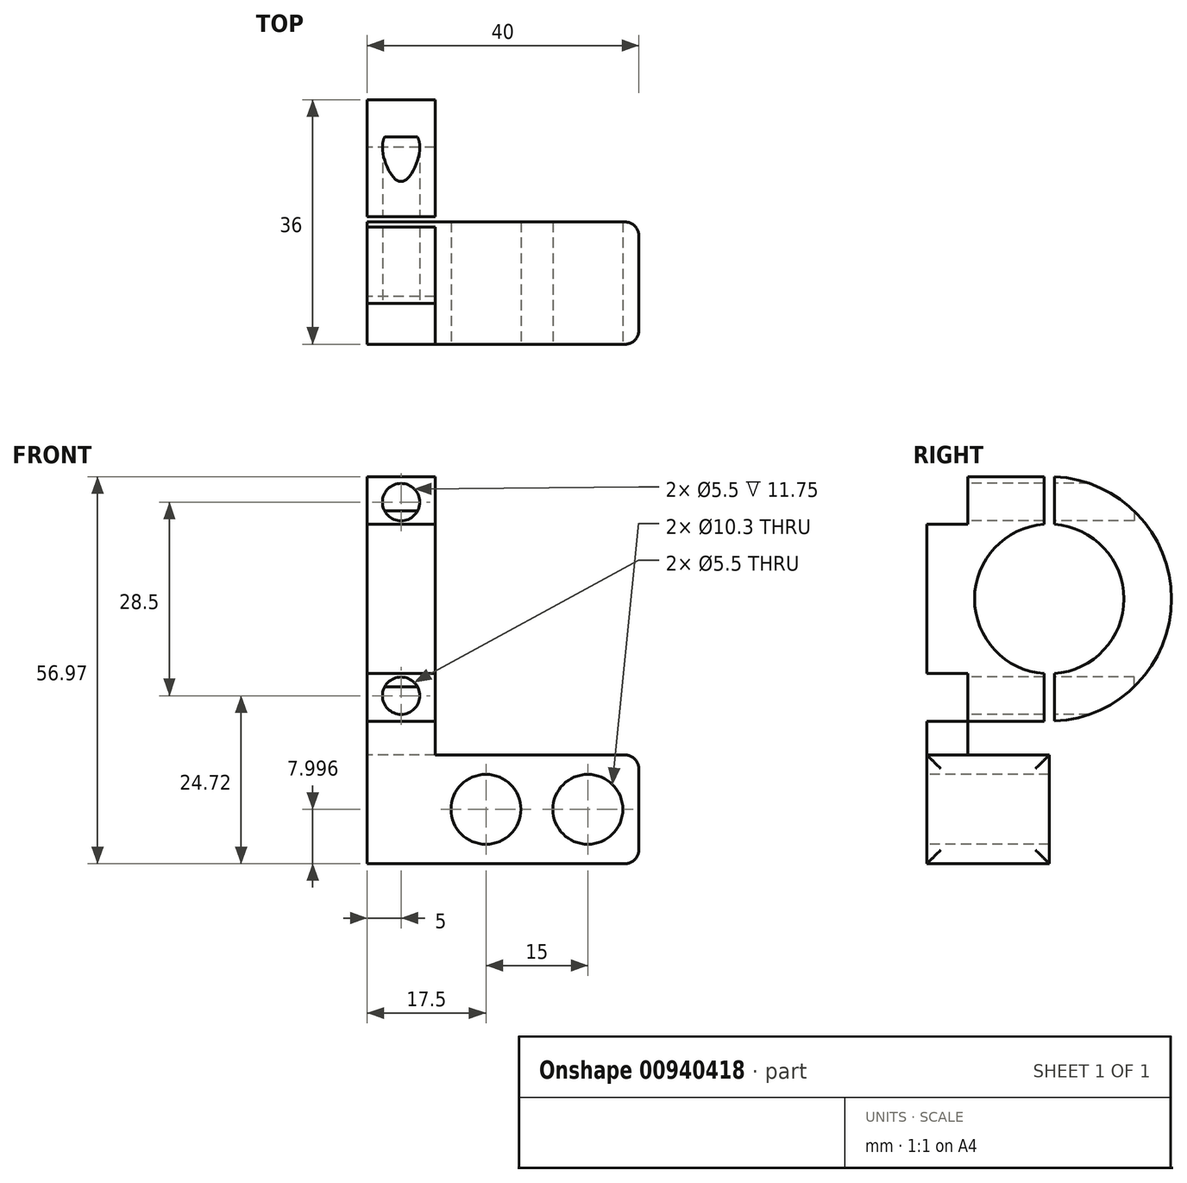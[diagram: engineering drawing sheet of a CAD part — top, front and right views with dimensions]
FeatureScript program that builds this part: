
annotation { "Feature Type Name" : "Feature", "Feature Type Description" : "" }
export const myFeature = defineFeature(function(context is Context, id is Id, definition is map)
    precondition{}
    {
        {
            var Q0;
            Q0=qCreatedBy(makeId("Right.planeOp"),FACE);
            var sketch = newSketch(context, id + "F0", { "sketchPlane" : qUnion([Q0])});
            skArc(sketch, "E0", {"start": v(-0.75, 10.97) * mm, "mid": v(-11, 0) * mm, "end": v(-0.75, -10.97) * mm});
            skArc(sketch, "E1", {"start": v(0.75, -17.98) * mm, "mid": v(18, 0) * mm, "end": v(0.75, 17.98) * mm});
            skLineSegment(sketch, "E2", {"start": v(-0.75, 18) * mm, "end": v(-12, 18) * mm});
            skLineSegment(sketch, "E3", {"start": v(-0.75, 18) * mm, "end": v(-0.75, 10.97) * mm});
            skLineSegment(sketch, "E4", {"start": v(0.75, 17.98) * mm, "end": v(0.75, 10.97) * mm});
            skLineSegment(sketch, "E5.trimOffspring", {"start": v(-0.75, -10.97) * mm, "end": v(-0.75, -18) * mm});
            skLineSegment(sketch, "E6.trimOffspring", {"start": v(0.75, -10.97) * mm, "end": v(0.75, -17.98) * mm});
            skArc(sketch, "E7.trimOffspring", {"start": v(0.75, -10.97) * mm, "mid": v(11, 0) * mm, "end": v(0.75, 10.97) * mm});
            skPoint(sketch, "E8.orphan", {"position": v(0, 18) * mm});
            skLineSegment(sketch, "E9.top", {"start": v(-18, 10.97) * mm, "end": v(-12, 10.97) * mm});
            skLineSegment(sketch, "E9.right", {"start": v(-12, 18) * mm, "end": v(-12, 10.97) * mm});
            skLineSegment(sketch, "E10", {"start": v(-0.75, -18) * mm, "end": v(-12, -18) * mm});
            skLineSegment(sketch, "E11", {"start": v(-12, -18) * mm, "end": v(-12, -10.97) * mm});
            skLineSegment(sketch, "E12", {"start": v(-12, -10.97) * mm, "end": v(-18, -10.97) * mm});
            skLineSegment(sketch, "E13", {"start": v(-18, -10.97) * mm, "end": v(-18, 10.97) * mm});
            skLineSegment(sketch, "E14", {"start": v(0, 0) * mm, "end": v(-49.75, 0) * mm, "construction": true});
            skPoint(sketch, "E14.endSnap0", {"position": v(-11, 0) * mm});
            skSolve(sketch);
        }
        {
            var Q0;
            Q0=qSketchRegion(id+"F0",true);
            extrude(context, id + "F1", {"entities" : qUnion([Q0]), "endBound" : BoundingType.SYMMETRIC, "depth" : 10 * mm, "offsetDistance" : 25 * mm});
        }
        {
            var Q0;
            Q0=qCreatedBy(makeId("Front.planeOp"),FACE);
            var sketch = newSketch(context, id + "F2", { "sketchPlane" : qUnion([Q0])});
            skCircle(sketch, "E15", {"center": v(0, 14.25) * mm, "radius": 2.75 * mm});
            skCircle(sketch, "E16", {"center": v(0, -14.25) * mm, "radius": 2.75 * mm});
            skSolve(sketch);
        }
        {
            var Q0;
            Q0=qSketchRegion(id+"F2",true);
            var Q1;
            Q1=makeQuery(id+"F1.opExtrude","SWEPT_FACE",FACE,{"disambiguationData":[OSD([sQuery(id+"F0.wireOp",EDGE,"E11")])]});
            extrude(context, id + "F3", {"entities" : qUnion([Q0]), "operationType" : NewBodyOperationType.REMOVE, "endBound" : BoundingType.SYMMETRIC, "oppositeDirection" : true, "depth" : 25 * mm, "endBoundEntityFace" : qUnion([Q1]), "offsetDistance" : 25 * mm});
        }
        {
            var Q0;
            Q0=makeQuery(id+"F1.opExtrude","SWEPT_FACE",FACE,{"disambiguationData":[OSD([sQuery(id+"F0.wireOp",EDGE,"E11")])]});
            var sketch = newSketch(context, id + "F4", { "sketchPlane" : qUnion([Q0])});
            skLineSegment(sketch, "E17", {"start": v(-5, -10.97) * mm, "end": v(5, -10.97) * mm});
            skLineSegment(sketch, "E18", {"start": v(5, -10.97) * mm, "end": v(5, -22.97) * mm});
            skLineSegment(sketch, "E19", {"start": v(5, -22.97) * mm, "end": v(35, -22.97) * mm});
            skLineSegment(sketch, "E20", {"start": v(35, -22.97) * mm, "end": v(35, -38.97) * mm});
            skLineSegment(sketch, "E21", {"start": v(35, -38.97) * mm, "end": v(-5, -38.97) * mm});
            skLineSegment(sketch, "E22", {"start": v(-5, -38.97) * mm, "end": v(-5, -10.97) * mm});
            skLineSegment(sketch, "E23", {"start": v(5, -10.97) * mm, "end": v(-5, -10.97) * mm});
            skLineSegment(sketch, "E24", {"start": v(-5, -10.97) * mm, "end": v(-5, -38.97) * mm});
            skLineSegment(sketch, "E25", {"start": v(5, -22.97) * mm, "end": v(-5, -22.97) * mm});
            skSolve(sketch);
        }
        {
            var Q0;
            {var subQ2=sQuery(id+"F4.wireOp",EDGE,"E25");Q0=makeQuery(id+"F4.imprint","IMPRINT",FACE,{"disambiguationData":[TD([[makeQuery(id+"F4.imprint","IMPRINT",EDGE,{"derivedFrom":subQ2}),-1.0]])]});}
            var Q1;
            {var subQ3=sQuery(id+"F4.wireOp",EDGE,"E23");Q1=makeQuery(id+"F4.imprint","IMPRINT",FACE,{"disambiguationData":[TD([[makeQuery(id+"F4.imprint","IMPRINT",EDGE,{"derivedFrom":subQ3}),1.0]])]});}
            var Q2;
            Q2=makeQuery(id+"F1.opExtrude","SWEPT_FACE",FACE,{"disambiguationData":[OSD([sQuery(id+"F0.wireOp",EDGE,"E13")])]});
            extrude(context, id + "F5", {"entities" : qUnion([Q0, Q1]), "endBound" : BoundingType.UP_TO_SURFACE, "depth" : 25 * mm, "endBoundEntityFace" : qUnion([Q2]), "offsetDistance" : 25 * mm});
        }
        {
            var Q0;
            Q0=makeQuery(id+"F4.imprint","IMPRINT",FACE,{"disambiguationData":[TD([[makeQuery(id+"F4.imprint","IMPRINT",EDGE,{"derivedFrom":sQuery(id+"F4.wireOp",EDGE,"E19")}),-1.0]])]});
            var Q1;
            Q1=makeQuery(id+"F1.opExtrude","SWEPT_FACE",FACE,{"disambiguationData":[OSD([sQuery(id+"F0.wireOp",EDGE,"E13")])]});
            extrude(context, id + "F6", {"entities" : qUnion([Q0]), "operationType" : NewBodyOperationType.ADD, "endBound" : BoundingType.UP_TO_SURFACE, "depth" : 25 * mm, "endBoundEntityFace" : qUnion([Q1]), "offsetDistance" : 25 * mm, "hasSecondDirection" : true, "secondDirectionOppositeDirection" : true, "secondDirectionDepth" : 12 * mm});
        }
        {
            var Q0;
            {var subQ0=sQuery(id+"F4.wireOp",EDGE,"E25");var subQ1=sQuery(id+"F4.wireOp",EDGE,"E24");Q0=makeQuery(id+"F6.boolean.opBoolean","MERGE",FACE,{"derivedFrom":[makeQuery(id+"F5.opExtrude","CAP_FACE",FACE,{"disambiguationData":[OSD([sQuery(id+"F0.wireOp",EDGE,"E11"),sQuery(id+"F2.wireOp",EDGE,"E16"),sQuery(id+"F4.wireOp",EDGE,"E18"),sQuery(id+"F4.wireOp",EDGE,"E23"),subQ1,subQ0])],"isStart":false}),makeQuery(id+"F6.opExtrude","CAP_FACE",FACE,{"disambiguationData":[OSD([sQuery(id+"F4.wireOp",EDGE,"E19"),sQuery(id+"F4.wireOp",EDGE,"E20"),sQuery(id+"F4.wireOp",EDGE,"E21"),subQ1,subQ0])],"isStart":false})]});}
            var sketch = newSketch(context, id + "F7", { "sketchPlane" : qUnion([Q0])});
            skLineSegment(sketch, "E26", {"start": v(5, -22.97) * mm, "end": v(5, -38.97) * mm, "construction": true});
            skLineSegment(sketch, "E27", {"start": v(5, -38.97) * mm, "end": v(35, -38.97) * mm, "construction": true});
            skLineSegment(sketch, "E28", {"start": v(35, -38.97) * mm, "end": v(35, -22.97) * mm, "construction": true});
            skLineSegment(sketch, "E29", {"start": v(35, -22.97) * mm, "end": v(5, -22.97) * mm, "construction": true});
            skLineSegment(sketch, "E30", {"start": v(20, -22.97) * mm, "end": v(20, -38.97) * mm, "construction": true});
            skLineSegment(sketch, "E31", {"start": v(20, -38.97) * mm, "end": v(35, -22.97) * mm, "construction": true});
            skLineSegment(sketch, "E32", {"start": v(20, -22.97) * mm, "end": v(35, -38.97) * mm, "construction": true});
            skLineSegment(sketch, "E33", {"start": v(20, -22.97) * mm, "end": v(5, -38.97) * mm, "construction": true});
            skLineSegment(sketch, "E34", {"start": v(5, -22.97) * mm, "end": v(20, -38.97) * mm, "construction": true});
            skPoint(sketch, "E35", {"position": v(12.5, -30.97) * mm});
            skPoint(sketch, "E36", {"position": v(27.5, -30.97) * mm});
            skCircle(sketch, "E37", {"center": v(12.5, -30.97) * mm, "radius": 5.15 * mm});
            skCircle(sketch, "E38", {"center": v(27.5, -30.97) * mm, "radius": 5.15 * mm});
            skSolve(sketch);
        }
        {
            var Q0;
            Q0=makeQuery(id+"F7.imprint","IMPRINT",FACE,{"disambiguationData":[TD([[makeQuery(id+"F7.imprint","IMPRINT",EDGE,{"derivedFrom":sQuery(id+"F7.wireOp",EDGE,"E37")}),1.0]])]});
            var Q1;
            Q1=makeQuery(id+"F6.opExtrude","CAP_FACE",FACE,{"disambiguationData":[OSD([sQuery(id+"F4.wireOp",EDGE,"E19"),sQuery(id+"F4.wireOp",EDGE,"E20"),sQuery(id+"F4.wireOp",EDGE,"E21"),sQuery(id+"F4.wireOp",EDGE,"E24"),sQuery(id+"F4.wireOp",EDGE,"E25")])],"isStart":true});
            extrude(context, id + "F8", {"entities" : qUnion([Q0]), "operationType" : NewBodyOperationType.REMOVE, "endBound" : BoundingType.UP_TO_SURFACE, "oppositeDirection" : true, "depth" : 25 * mm, "endBoundEntityFace" : qUnion([Q1]), "offsetDistance" : 25 * mm});
        }
        {
            var Q0;
            Q0=makeQuery(id+"F7.imprint","IMPRINT",FACE,{"disambiguationData":[TD([[makeQuery(id+"F7.imprint","IMPRINT",EDGE,{"derivedFrom":sQuery(id+"F7.wireOp",EDGE,"E38")}),1.0]])]});
            var Q1;
            Q1=makeQuery(id+"F6.opExtrude","CAP_FACE",FACE,{"disambiguationData":[OSD([sQuery(id+"F4.wireOp",EDGE,"E19"),sQuery(id+"F4.wireOp",EDGE,"E20"),sQuery(id+"F4.wireOp",EDGE,"E21"),sQuery(id+"F4.wireOp",EDGE,"E24"),sQuery(id+"F4.wireOp",EDGE,"E25")])],"isStart":true});
            extrude(context, id + "F9", {"entities" : qUnion([Q0]), "operationType" : NewBodyOperationType.REMOVE, "endBound" : BoundingType.UP_TO_SURFACE, "oppositeDirection" : true, "depth" : 25 * mm, "endBoundEntityFace" : qUnion([Q1]), "offsetDistance" : 25 * mm});
        }
        {
            var Q0;
            Q0=makeQuery(id+"F7.imprint","IMPRINT",FACE,{"disambiguationData":[TD([[makeQuery(id+"F7.imprint","IMPRINT",EDGE,{"derivedFrom":sQuery(id+"F7.wireOp",EDGE,"E38")}),1.0]])]});
            var Q1;
            Q1=sQuery(id+"F7.wireOp",EDGE,"E38");
            extrude(context, id + "F10", {"entities" : qUnion([Q0]), "bodyType" : ToolBodyType.SURFACE, "surfaceEntities" : qUnion([Q1]), "oppositeDirection" : true, "depth" : 25 * mm, "offsetDistance" : 25 * mm, "hasSecondDirection" : true, "secondDirectionOppositeDirection" : false, "secondDirectionDepth" : 5 * mm});
        }
        {
            var Q0;
            Q0=makeQuery(id+"F6.opExtrude","CAP_EDGE",EDGE,{"disambiguationData":[OSD([sQuery(id+"F4.wireOp",EDGE,"E20")])],"isStart":false});
            var Q1;
            Q1=makeQuery(id+"F6.opExtrude","CAP_EDGE",EDGE,{"disambiguationData":[OSD([sQuery(id+"F4.wireOp",EDGE,"E20")])],"isStart":true});
            var Q2;
            Q2=makeQuery(id+"F6.opExtrude","SWEPT_EDGE",EDGE,{"disambiguationData":[OSD([sQuery(id+"F4.wireOp",EDGE,"E20"),sQuery(id+"F4.wireOp",EDGE,"E21")])]});
            var Q3;
            Q3=makeQuery(id+"F6.opExtrude","SWEPT_EDGE",EDGE,{"disambiguationData":[OSD([sQuery(id+"F4.wireOp",EDGE,"E19"),sQuery(id+"F4.wireOp",EDGE,"E20")])]});
            var Q4;
            {var subQ0=sQuery(id+"F4.wireOp",EDGE,"E24");Q4=makeQuery(id+"F6.boolean.opBoolean","MERGE",EDGE,{"derivedFrom":[makeQuery(id+"F5.opExtrude","CAP_EDGE",EDGE,{"disambiguationData":[OSD([subQ0])],"isStart":false}),makeQuery(id+"F6.opExtrude","CAP_EDGE",EDGE,{"disambiguationData":[OSD([subQ0])],"isStart":false})]});}
            fillet(context, id + "F11", {"entities" : qUnion([Q0, Q1, Q2, Q3, Q4]), "tangentPropagation" : true, "radius" : 2 * mm, "defaultsChanged" : false, "vertexSettings" : [], "allowEdgeOverflow" : false});
        }
    });
